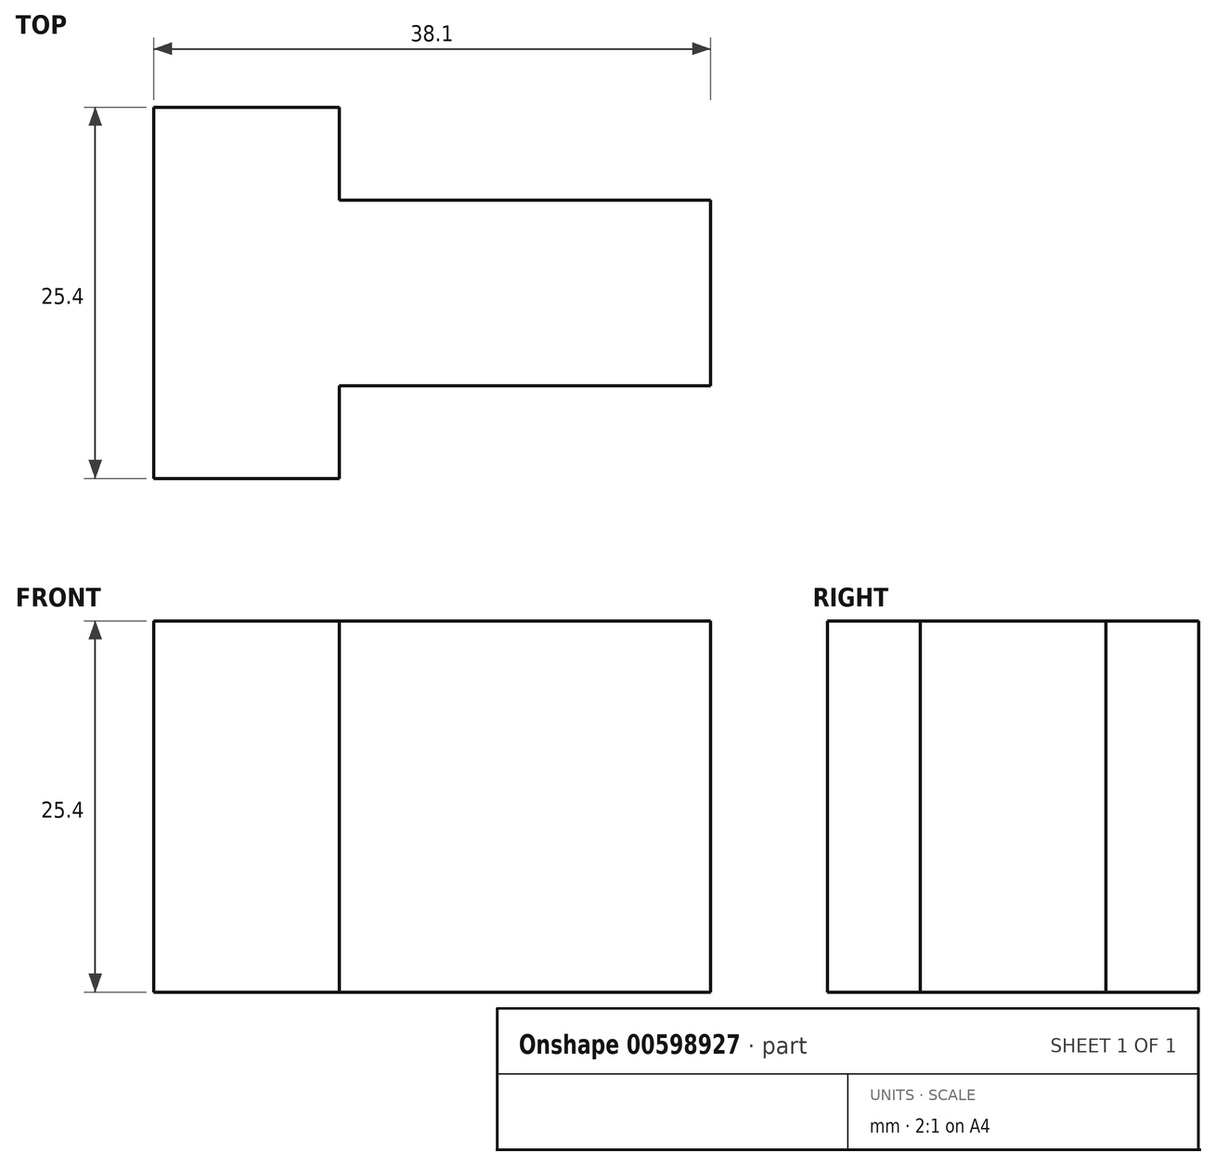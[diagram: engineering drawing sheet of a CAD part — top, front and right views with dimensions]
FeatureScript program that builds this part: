
annotation { "Feature Type Name" : "Feature", "Feature Type Description" : "" }
export const myFeature = defineFeature(function(context is Context, id is Id, definition is map)
    precondition{}
    {
        {
            var Q0;
            Q0=qCreatedBy(makeId("Top.planeOp"),FACE);
            var sketch = newSketch(context, id + "F0", { "sketchPlane" : qUnion([Q0])});
            skLineSegment(sketch, "E0", {"start": v(0, 0) * mm, "end": v(0, -12.7) * mm});
            skLineSegment(sketch, "E1", {"start": v(0, 0) * mm, "end": v(0, 12.7) * mm});
            skLineSegment(sketch, "E2", {"start": v(0, 12.7) * mm, "end": v(12.7, 12.7) * mm});
            skLineSegment(sketch, "E3", {"start": v(0, -12.7) * mm, "end": v(12.7, -12.7) * mm});
            skLineSegment(sketch, "E4", {"start": v(12.7, -12.7) * mm, "end": v(12.7, -6.35) * mm});
            skLineSegment(sketch, "E5", {"start": v(12.7, 12.7) * mm, "end": v(12.7, 6.35) * mm});
            skLineSegment(sketch, "E6", {"start": v(12.7, 6.35) * mm, "end": v(38.1, 6.35) * mm});
            skLineSegment(sketch, "E7", {"start": v(38.1, 6.35) * mm, "end": v(38.1, -6.35) * mm});
            skLineSegment(sketch, "E8", {"start": v(38.1, -6.35) * mm, "end": v(12.7, -6.35) * mm});
            skSolve(sketch);
        }
        {
            var Q0;
            Q0 = qSketchRegion(id + "F0", true);
            extrude(context, id + "F1", {"entities" : qUnion([Q0]), "depth" : 25.4 * mm, "offsetDistance" : 25.4 * mm});
        }
    });
